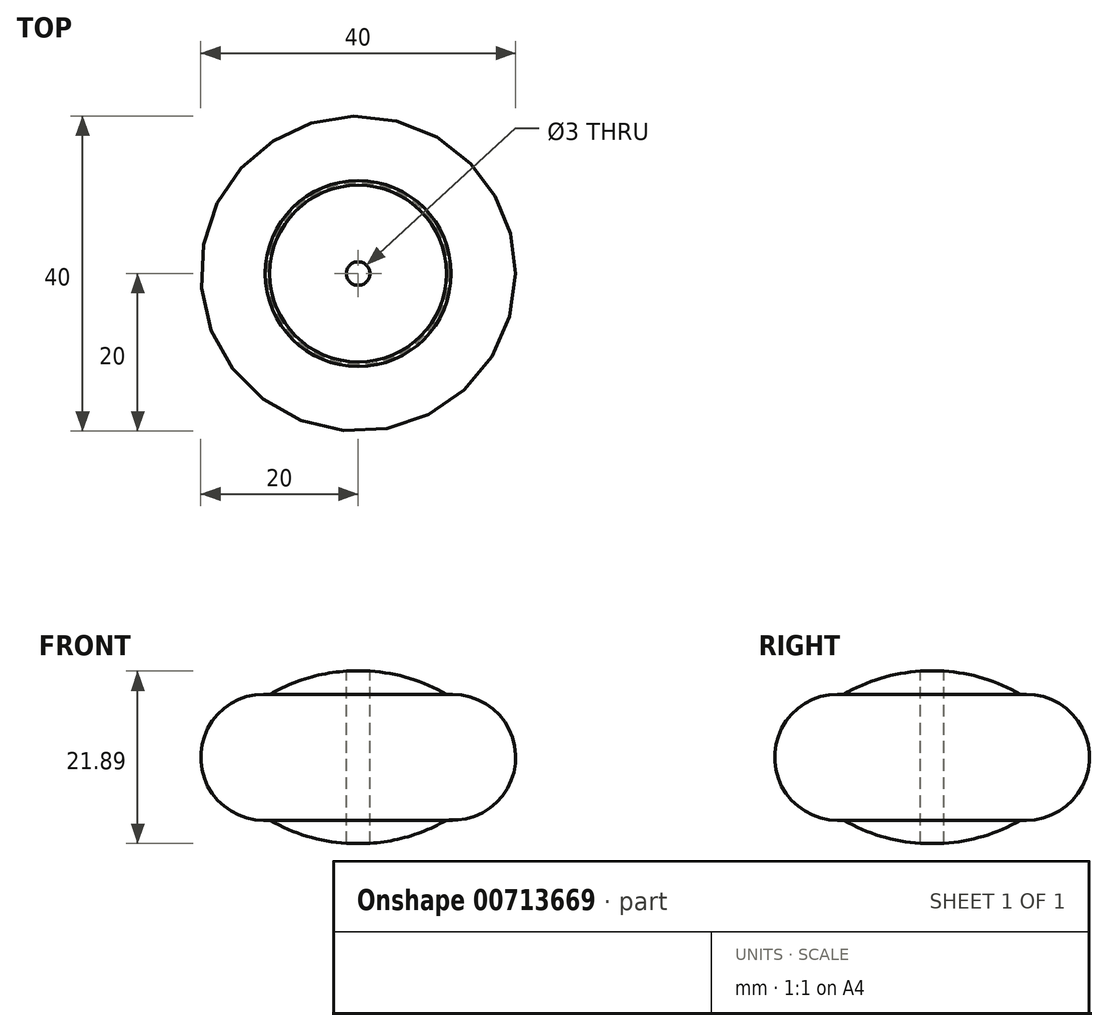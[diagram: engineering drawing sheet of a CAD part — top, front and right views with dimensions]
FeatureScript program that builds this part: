
annotation { "Feature Type Name" : "Feature", "Feature Type Description" : "" }
export const myFeature = defineFeature(function(context is Context, id is Id, definition is map)
    precondition{}
    {
        {
            var Q0;
            Q0=qCreatedBy(makeId("Front.planeOp"),FACE);
            var sketch = newSketch(context, id + "F0", { "sketchPlane" : qUnion([Q0])});
            skArc(sketch, "E0", {"start": v(-11.23, -7.99) * mm, "mid": v(-5.81, -10.22) * mm, "end": v(0, -10.99) * mm});
            skLineSegment(sketch, "E1", {"start": v(0, 0) * mm, "end": v(1105.39, 0) * mm, "construction": true});
            skLineSegment(sketch, "E2", {"start": v(0, 0) * mm, "end": v(0, 946.63) * mm, "construction": true});
            skArc(sketch, "E3", {"start": v(-11.81, 8) * mm, "mid": v(-20, -0.15) * mm, "end": v(-11.51, -7.99) * mm});
            skLineSegment(sketch, "E4", {"start": v(-11.81, 8) * mm, "end": v(-11.23, 8) * mm});
            skLineSegment(sketch, "E5", {"start": v(-12.5, -7.98) * mm, "end": v(-11.23, -7.99) * mm});
            skArc(sketch, "E6.trimOffspring", {"start": v(0, 11) * mm, "mid": v(-5.8, 10.24) * mm, "end": v(-11.23, 8) * mm});
            skLineSegment(sketch, "E7", {"start": v(0, 11) * mm, "end": v(0, -10.99) * mm});
            skPoint(sketch, "E8.center.orphan", {"position": v(12, 0) * mm});
            skSolve(sketch);
        }
        {
            var Q0;
            Q0=qSketchRegion(id+"F0",true);
            var Q1;
            Q1=sQuery(id+"F0.wireOp",EDGE,"E7");
            revolve(context, id + "F1", {"surfaceOperationType" : NewSurfaceOperationType.NEW, "entities" : qUnion([Q0]), "axis" : qUnion([Q1]), "revolveType" : RevolveType.FULL});
        }
        {
            var Q0;
            Q0=qCreatedBy(makeId("Top.planeOp"),FACE);
            var sketch = newSketch(context, id + "F2", { "sketchPlane" : qUnion([Q0])});
            skCircle(sketch, "E9", {"center": v(0, 0) * mm, "radius": 1.5 * mm});
            skSolve(sketch);
        }
        {
            var Q0;
            Q0=qSketchRegion(id+"F2",true);
            extrude(context, id + "F3", {"entities" : qUnion([Q0]), "operationType" : NewBodyOperationType.REMOVE, "endBound" : BoundingType.THROUGH_ALL, "oppositeDirection" : true, "depth" : 25.4 * mm, "offsetDistance" : 25.4 * mm, "hasSecondDirection" : true, "secondDirectionBound" : SecondDirectionBoundingType.THROUGH_ALL, "secondDirectionOppositeDirection" : false, "secondDirectionDepth" : 25.4 * mm});
        }
    });
